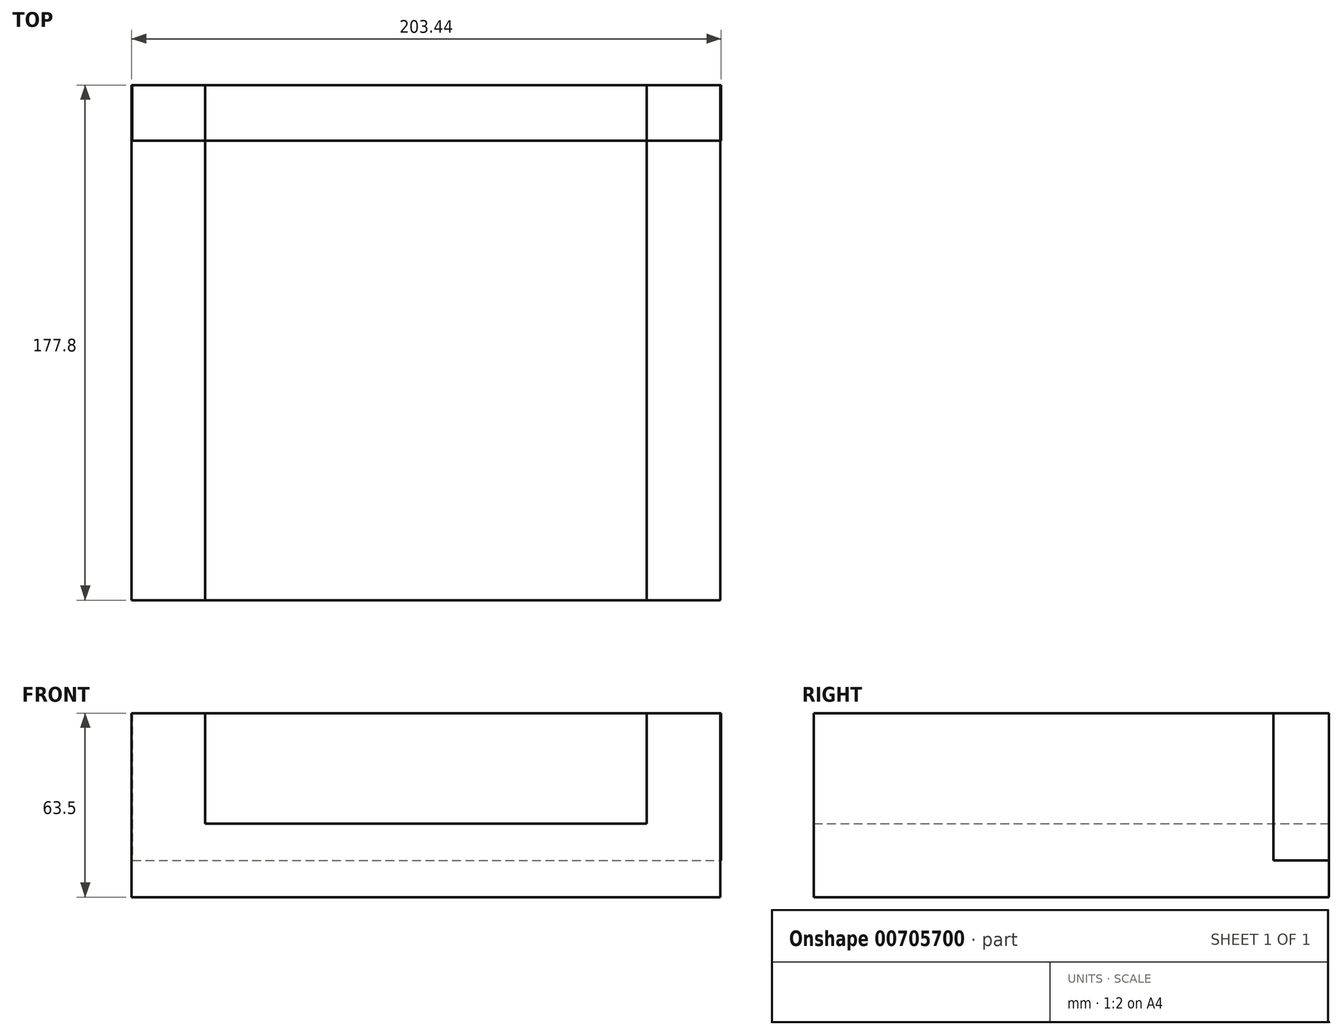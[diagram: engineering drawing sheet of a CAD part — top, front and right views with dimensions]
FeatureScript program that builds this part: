
annotation { "Feature Type Name" : "Feature", "Feature Type Description" : "" }
export const myFeature = defineFeature(function(context is Context, id is Id, definition is map)
    precondition{}
    {
        {
            var Q0;
            Q0=qCreatedBy(makeId("Front.planeOp"),FACE);
            var sketch = newSketch(context, id + "F0", { "sketchPlane" : qUnion([Q0])});
            skLineSegment(sketch, "E0.bottom", {"start": v(-101.6, -12.7) * mm, "end": v(101.6, -12.7) * mm});
            skLineSegment(sketch, "E0.top", {"start": v(-101.6, 12.7) * mm, "end": v(101.6, 12.7) * mm});
            skLineSegment(sketch, "E0.left", {"start": v(-101.6, -12.7) * mm, "end": v(-101.6, 12.7) * mm});
            skLineSegment(sketch, "E0.right", {"start": v(101.6, -12.7) * mm, "end": v(101.6, 12.7) * mm});
            skPoint(sketch, "E0.middle", {"position": v(0, 0) * mm});
            skLineSegment(sketch, "E1.bottom", {"start": v(-101.6, -12.7) * mm, "end": v(-76.2, -12.7) * mm});
            skLineSegment(sketch, "E2.bottom", {"start": v(101.6, -12.7) * mm, "end": v(76.2, -12.7) * mm});
            skLineSegment(sketch, "E3.top", {"start": v(101.6, 50.8) * mm, "end": v(76.2, 50.8) * mm});
            skLineSegment(sketch, "E3.left", {"start": v(101.6, -12.7) * mm, "end": v(101.6, 50.8) * mm});
            skLineSegment(sketch, "E3.right", {"start": v(76.2, -12.7) * mm, "end": v(76.2, 50.8) * mm});
            skLineSegment(sketch, "E4.top", {"start": v(-101.6, 50.8) * mm, "end": v(-76.2, 50.8) * mm});
            skLineSegment(sketch, "E4.left", {"start": v(-101.6, -12.7) * mm, "end": v(-101.6, 50.8) * mm});
            skLineSegment(sketch, "E4.right", {"start": v(-76.2, -12.7) * mm, "end": v(-76.2, 50.8) * mm});
            skSolve(sketch);
        }
        {
            var Q0;
            {var subQ5=sQuery(id+"F0.wireOp",EDGE,"E1.top");Q0=makeQuery(id+"F0.imprint","IMPRINT",FACE,{"disambiguationData":[TD([[makeQuery(id+"F0.imprint","IMPRINT",EDGE,{"derivedFrom":subQ5}),-1.0]])]});}
            var Q1;
            {var subQ5=sQuery(id+"F0.wireOp",EDGE,"E1.bottom");Q1=makeQuery(id+"F0.imprint","IMPRINT",FACE,{"disambiguationData":[TD([[makeQuery(id+"F0.imprint","IMPRINT",EDGE,{"derivedFrom":subQ5}),1.0]])]});}
            var Q2;
            {var subQ0=sQuery(id+"F0.wireOp",EDGE,"E0.bottom");Q2=makeQuery(id+"F0.imprint","IMPRINT",FACE,{"disambiguationData":[TD([[makeQuery(id+"F0.imprint","IMPRINT",EDGE,{"derivedFrom":subQ0}),1.0]])]});}
            var Q3;
            {var subQ5=sQuery(id+"F0.wireOp",EDGE,"E2.top");Q3=makeQuery(id+"F0.imprint","IMPRINT",FACE,{"disambiguationData":[TD([[makeQuery(id+"F0.imprint","IMPRINT",EDGE,{"derivedFrom":subQ5}),1.0]])]});}
            var Q4;
            {var subQ5=sQuery(id+"F0.wireOp",EDGE,"E2.bottom");Q4=makeQuery(id+"F0.imprint","IMPRINT",FACE,{"disambiguationData":[TD([[makeQuery(id+"F0.imprint","IMPRINT",EDGE,{"derivedFrom":subQ5}),-1.0]])]});}
            var Q5;
            {var subQ5=sQuery(id+"F0.wireOp",EDGE,"E3.top");Q5=makeQuery(id+"F0.imprint","IMPRINT",FACE,{"disambiguationData":[TD([[makeQuery(id+"F0.imprint","IMPRINT",EDGE,{"derivedFrom":subQ5}),1.0]])]});}
            var Q6;
            {var subQ5=sQuery(id+"F0.wireOp",EDGE,"E2.bottom");Q6=makeQuery(id+"F0.imprint","IMPRINT",FACE,{"disambiguationData":[TD([[makeQuery(id+"F0.imprint","IMPRINT",EDGE,{"derivedFrom":subQ5}),-1.0]])]});}
            var Q7;
            {var subQ5=sQuery(id+"F0.wireOp",EDGE,"E4.top");Q7=makeQuery(id+"F0.imprint","IMPRINT",FACE,{"disambiguationData":[TD([[makeQuery(id+"F0.imprint","IMPRINT",EDGE,{"derivedFrom":subQ5}),-1.0]])]});}
            var Q8;
            {var subQ5=sQuery(id+"F0.wireOp",EDGE,"E1.bottom");Q8=makeQuery(id+"F0.imprint","IMPRINT",FACE,{"disambiguationData":[TD([[makeQuery(id+"F0.imprint","IMPRINT",EDGE,{"derivedFrom":subQ5}),1.0]])]});}
            extrude(context, id + "F1", {"entities" : qUnion([Q0, Q1, Q2, Q3, Q4, Q5, Q6, Q7, Q8]), "depth" : 177.8 * mm, "offsetDistance" : 25.4 * mm});
        }
        {
            var Q0;
            Q0=qCreatedBy(makeId("Top.planeOp"),FACE);
            var sketch = newSketch(context, id + "F2", { "sketchPlane" : qUnion([Q0])});
            skLineSegment(sketch, "E5.bottom", {"start": v(-101.36, 0) * mm, "end": v(101.84, 0) * mm});
            skLineSegment(sketch, "E5.top", {"start": v(-101.36, -19.23) * mm, "end": v(101.84, -19.23) * mm});
            skLineSegment(sketch, "E5.left", {"start": v(-101.36, 0) * mm, "end": v(-101.36, -19.23) * mm});
            skLineSegment(sketch, "E5.right", {"start": v(101.84, 0) * mm, "end": v(101.84, -19.23) * mm});
            skSolve(sketch);
        }
        {
            var Q0;
            Q0=makeQuery(id+"F2.imprint","IMPRINT",FACE,{"disambiguationData":[TD([[makeQuery(id+"F2.imprint","IMPRINT",EDGE,{"derivedFrom":sQuery(id+"F2.wireOp",EDGE,"E5.bottom")}),-1.0]])]});
            extrude(context, id + "F3", {"entities" : qUnion([Q0]), "depth" : 50.8 * mm, "offsetDistance" : 25.4 * mm});
        }
    });
